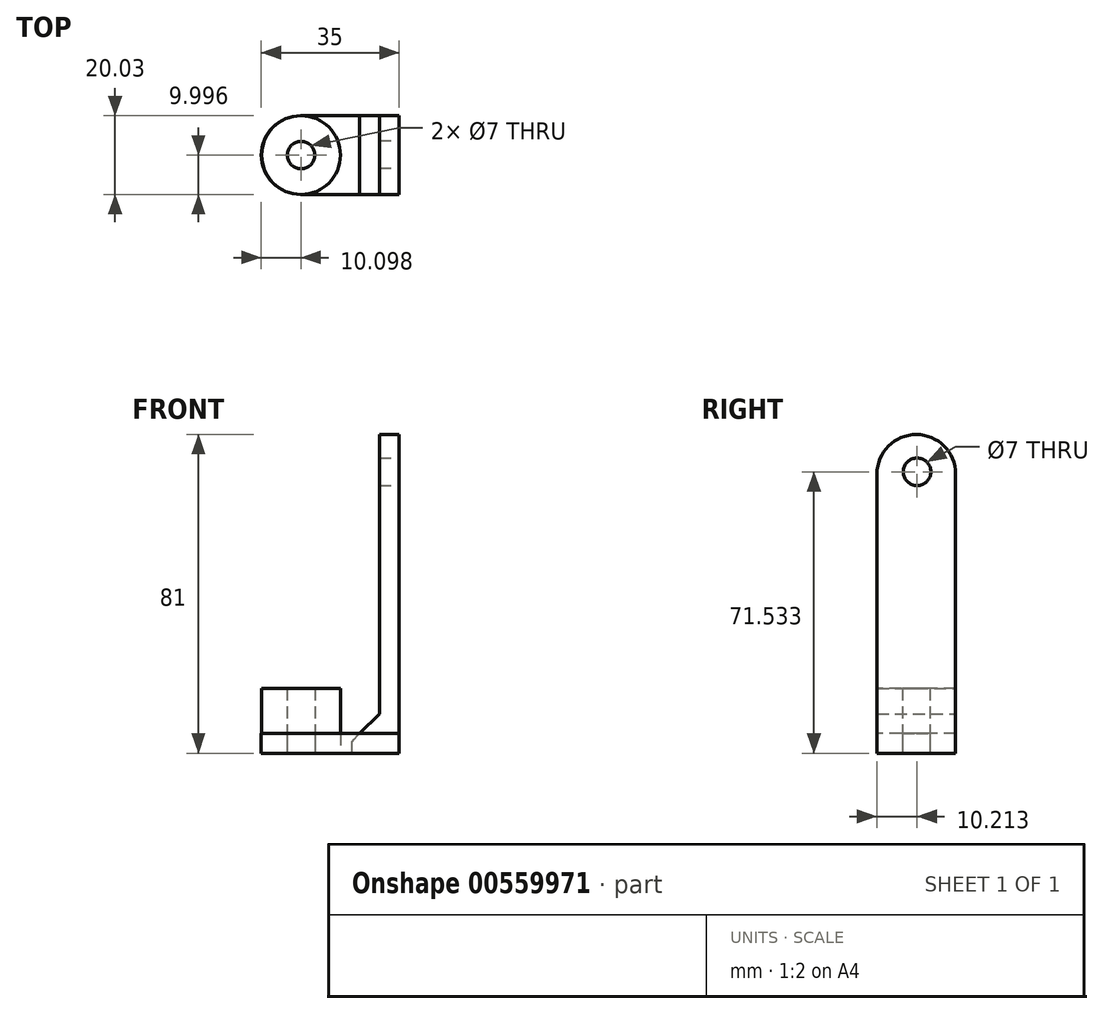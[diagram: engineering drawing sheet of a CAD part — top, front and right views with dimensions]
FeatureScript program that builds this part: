
annotation { "Feature Type Name" : "Feature", "Feature Type Description" : "" }
export const myFeature = defineFeature(function(context is Context, id is Id, definition is map)
    precondition{}
    {
        {
            var Q0;
            Q0=qCreatedBy(makeId("Top.planeOp"),FACE);
            var sketch = newSketch(context, id + "F0", { "sketchPlane" : qUnion([Q0])});
            skLineSegment(sketch, "E0.bottom", {"start": v(-46.2, 30.05) * mm, "end": v(-11.2, 30.05) * mm});
            skLineSegment(sketch, "E0.top", {"start": v(-46.2, 10.05) * mm, "end": v(-11.2, 10.05) * mm});
            skLineSegment(sketch, "E0.left", {"start": v(-46.2, 30.05) * mm, "end": v(-46.2, 10.05) * mm});
            skLineSegment(sketch, "E0.right", {"start": v(-11.2, 30.05) * mm, "end": v(-11.2, 10.05) * mm});
            skLineSegment(sketch, "E1", {"start": v(-46.2, 20.05) * mm, "end": v(-11.2, 20.05) * mm, "construction": true});
            skCircle(sketch, "E2", {"center": v(-36.1, 20.05) * mm, "radius": 3.5 * mm});
            skCircle(sketch, "E3", {"center": v(-36.1, 20.05) * mm, "radius": 10 * mm});
            skSolve(sketch);
        }
        {
            var Q0;
            Q0=makeQuery(id+"F0.imprint","IMPRINT",FACE,{"disambiguationData":[TD([[makeQuery(id+"F0.imprint","IMPRINT",EDGE,{"derivedFrom":sQuery(id+"F0.wireOp",EDGE,"E0.bottom")}),-1.0]])]});
            var Q1;
            Q1=makeQuery(id+"F0.imprint","IMPRINT",FACE,{"disambiguationData":[TD([[makeQuery(id+"F0.imprint","IMPRINT",EDGE,{"derivedFrom":sQuery(id+"F0.wireOp",EDGE,"E2")}),-1.0]])]});
            extrude(context, id + "F1", {"entities" : qUnion([Q0, Q1]), "depth" : 5 * mm, "offsetDistance" : 25 * mm});
        }
        {
            var Q0;
            Q0=makeQuery(id+"F1.opExtrude","SWEPT_EDGE",EDGE,{"disambiguationData":[OSD([sQuery(id+"F0.wireOp",EDGE,"E0.bottom"),sQuery(id+"F0.wireOp",EDGE,"E0.left")])]});
            var Q1;
            Q1=makeQuery(id+"F1.opExtrude","SWEPT_EDGE",EDGE,{"disambiguationData":[OSD([sQuery(id+"F0.wireOp",EDGE,"E0.top"),sQuery(id+"F0.wireOp",EDGE,"E0.left")])]});
            fillet(context, id + "F2", {"entities" : qUnion([Q0, Q1]), "radius" : 10 * mm, "tangentPropagation" : true, "allowEdgeOverflow" : false});
        }
        {
            var Q0;
            Q0=qCreatedBy(makeId("Top.planeOp"),FACE);
            var sketch = newSketch(context, id + "F3", { "sketchPlane" : qUnion([Q0])});
            skLineSegment(sketch, "E4.bottom", {"start": v(-11.2, 10.08) * mm, "end": v(-16.2, 10.08) * mm});
            skLineSegment(sketch, "E4.top", {"start": v(-11.2, 30.08) * mm, "end": v(-16.2, 30.08) * mm});
            skLineSegment(sketch, "E4.left", {"start": v(-11.2, 10.08) * mm, "end": v(-11.2, 30.08) * mm});
            skLineSegment(sketch, "E4.right", {"start": v(-16.2, 10.08) * mm, "end": v(-16.2, 30.08) * mm});
            skLineSegment(sketch, "E5.bottom", {"start": v(-16.2, 10.08) * mm, "end": v(-23.2, 10.08) * mm});
            skLineSegment(sketch, "E5.top", {"start": v(-16.2, 30.08) * mm, "end": v(-23.2, 30.08) * mm});
            skLineSegment(sketch, "E5.right", {"start": v(-23.2, 10.08) * mm, "end": v(-23.2, 30.08) * mm});
            skSolve(sketch);
        }
        {
            var Q0;
            Q0=makeQuery(id+"F3.imprint","IMPRINT",FACE,{"disambiguationData":[TD([[makeQuery(id+"F3.imprint","IMPRINT",EDGE,{"derivedFrom":sQuery(id+"F3.wireOp",EDGE,"E4.bottom")}),-1.0]])]});
            extrude(context, id + "F4", {"entities" : qUnion([Q0]), "depth" : 81 * mm, "offsetDistance" : 25 * mm, "hasSecondDirection" : true, "secondDirectionOppositeDirection" : false, "secondDirectionDepth" : 5 * mm});
        }
        {
            var Q0;
            Q0=qCreatedBy(makeId("Right.planeOp"),FACE);
            var sketch = newSketch(context, id + "F5", { "sketchPlane" : qUnion([Q0])});
            skLineSegment(sketch, "E6", {"start": v(20.26, 101.03) * mm, "end": v(20.26, 0) * mm, "construction": true});
            skCircle(sketch, "E7", {"center": v(20.26, 71.53) * mm, "radius": 3.5 * mm});
            skSolve(sketch);
        }
        {
            var Q0;
            Q0=makeQuery(id+"F5.imprint","IMPRINT",FACE,{"disambiguationData":[TD([[makeQuery(id+"F5.imprint","IMPRINT",EDGE,{"derivedFrom":sQuery(id+"F5.wireOp",EDGE,"E7")}),1.0]])]});
            extrude(context, id + "F6", {"entities" : qUnion([Q0]), "operationType" : NewBodyOperationType.REMOVE, "depth" : 79.3 * mm, "offsetDistance" : 25 * mm});
        }
        {
            var Q0;
            Q0=makeQuery(id+"F4.opExtrude","CAP_EDGE",EDGE,{"disambiguationData":[OSD([sQuery(id+"F3.wireOp",EDGE,"E4.bottom")])],"isStart":false});
            var Q1;
            Q1=makeQuery(id+"F4.opExtrude","CAP_EDGE",EDGE,{"disambiguationData":[OSD([sQuery(id+"F3.wireOp",EDGE,"E4.top")])],"isStart":false});
            fillet(context, id + "F7", {"entities" : qUnion([Q0, Q1]), "radius" : 10 * mm, "tangentPropagation" : true, "allowEdgeOverflow" : false});
        }
        {
            var Q0;
            Q0=makeQuery(id+"F0.imprint","IMPRINT",FACE,{"disambiguationData":[TD([[makeQuery(id+"F0.imprint","IMPRINT",EDGE,{"derivedFrom":sQuery(id+"F0.wireOp",EDGE,"E2")}),-1.0]])]});
            extrude(context, id + "F8", {"entities" : qUnion([Q0]), "depth" : 16.5 * mm, "offsetDistance" : 25 * mm});
        }
        {
            var Q0;
            Q0 = qSketchRegion(id + "F3", true);
            extrude(context, id + "F9", {"entities" : qUnion([Q0]), "operationType" : NewBodyOperationType.ADD, "depth" : 10 * mm, "offsetDistance" : 25 * mm});
        }
        {
            var Q0;
            Q0=makeQuery(id+"F9.opExtrude","CAP_EDGE",EDGE,{"disambiguationData":[OSD([sQuery(id+"F3.wireOp",EDGE,"E5.right")])],"isStart":false});
            chamfer(context, id + "F10", {"entities" : qUnion([Q0]), "width" : 7 * mm, "tangentPropagation" : true});
        }
        {
            var Q0;
            Q0=makeQuery(id+"F5.imprint","IMPRINT",FACE,{"disambiguationData":[TD([[makeQuery(id+"F5.imprint","IMPRINT",EDGE,{"derivedFrom":sQuery(id+"F5.wireOp",EDGE,"E7")}),1.0]])]});
            extrude(context, id + "F11", {"entities" : qUnion([Q0]), "operationType" : NewBodyOperationType.REMOVE, "oppositeDirection" : true, "depth" : 55.6 * mm, "offsetDistance" : 25 * mm});
        }
    });
